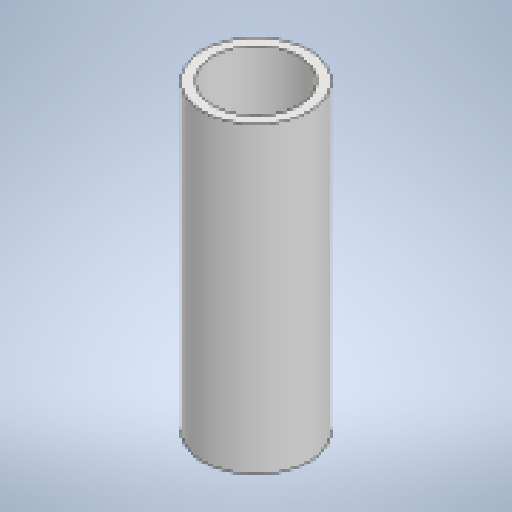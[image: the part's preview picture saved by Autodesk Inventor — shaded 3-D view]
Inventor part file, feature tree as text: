
AUTODESK INVENTOR PART (.ipt)
format: ipt  version: 2025.1 (Build 291241020, 241B)  size: 169,472 bytes
history: native  units: mm
features: extrude x1, sketch x1
ambient origin geometry x8: Origin, YZ Plane, XZ Plane, XY Plane, X Axis, Y Axis, Z Axis, Center Point
bodies: Body1 (feature_tree)
feature tree (2):
  extrude  "Extrusion5"  Depth=60.0mm
  sketch  "Sketch11"  dims[d187=21.0mm d188=2.0mm d189=60.0mm d190=0.0mm]
